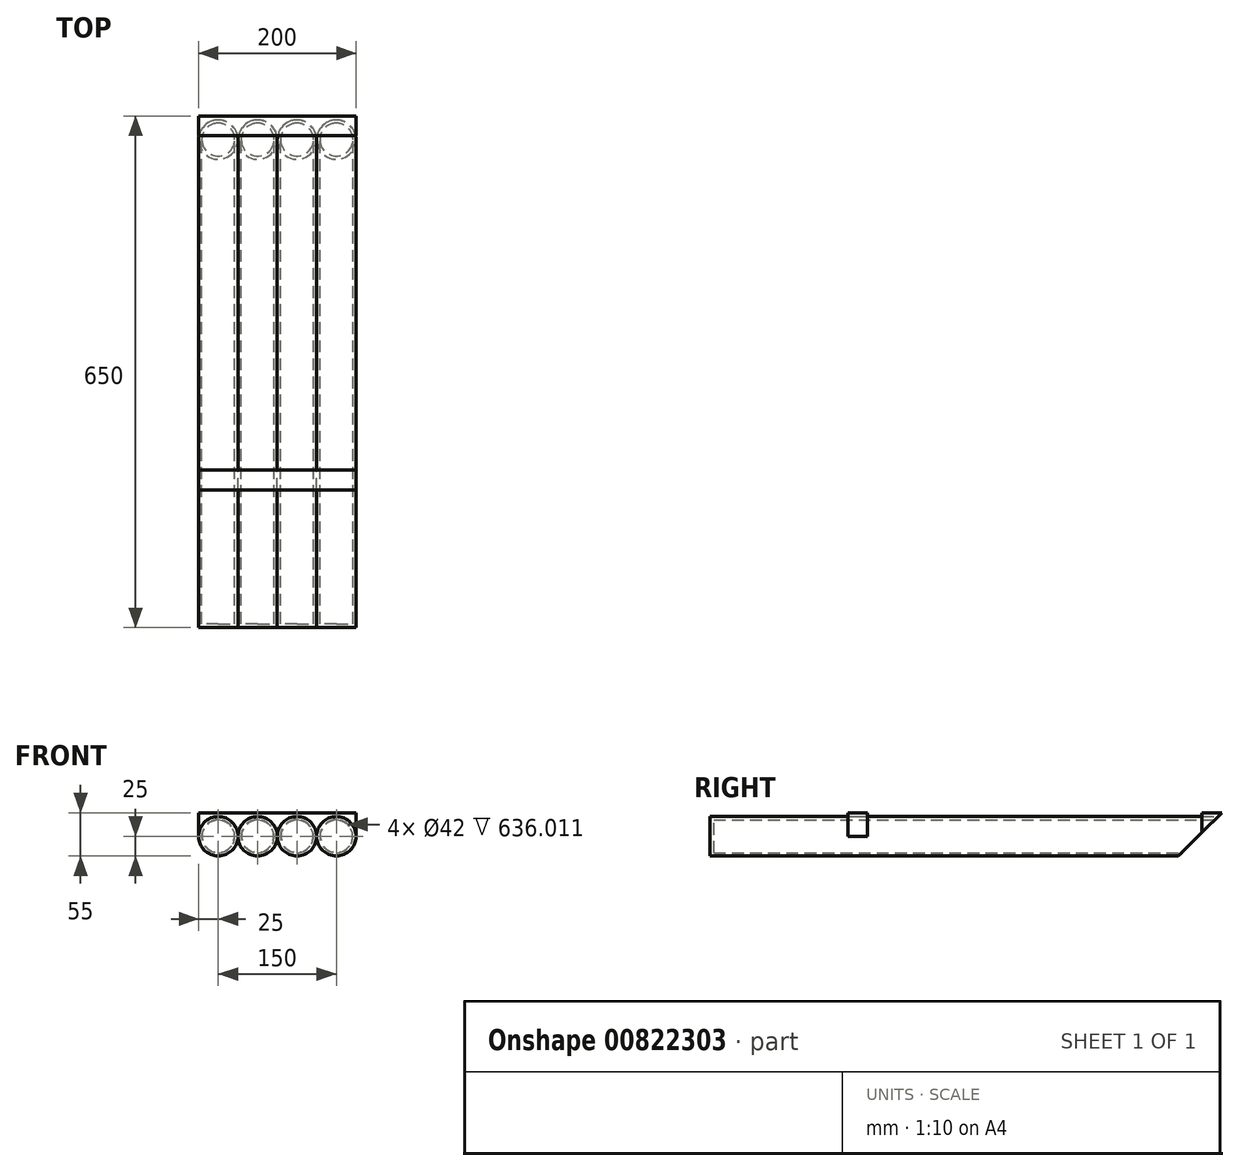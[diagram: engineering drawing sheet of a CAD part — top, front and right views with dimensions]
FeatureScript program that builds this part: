
annotation { "Feature Type Name" : "Feature", "Feature Type Description" : "" }
export const myFeature = defineFeature(function(context is Context, id is Id, definition is map)
    precondition{}
    {
        {
            var Q0;
            Q0=qCreatedBy(makeId("Front.planeOp"),FACE);
            var sketch = newSketch(context, id + "F0", { "sketchPlane" : qUnion([Q0])});
            skCircle(sketch, "E0", {"center": v(0, 0) * mm, "radius": 25 * mm});
            skCircle(sketch, "E1", {"center": v(50, 0) * mm, "radius": 25 * mm});
            skCircle(sketch, "E2", {"center": v(-50, 0) * mm, "radius": 25 * mm});
            skCircle(sketch, "E3", {"center": v(-100, 0) * mm, "radius": 25 * mm});
            skLineSegment(sketch, "E4", {"start": v(0, 0) * mm, "end": v(50, 0) * mm});
            skLineSegment(sketch, "E5", {"start": v(0, 0) * mm, "end": v(-50, 0) * mm});
            skLineSegment(sketch, "E6", {"start": v(-50, 0) * mm, "end": v(-100, 0) * mm});
            skCircle(sketch, "E7", {"center": v(50, 0) * mm, "radius": 21 * mm});
            skCircle(sketch, "E8", {"center": v(0, 0) * mm, "radius": 21 * mm});
            skCircle(sketch, "E9", {"center": v(-50, 0) * mm, "radius": 21 * mm});
            skCircle(sketch, "E10", {"center": v(-100, 0) * mm, "radius": 21 * mm});
            skSolve(sketch);
        }
        {
            var Q0;
            Q0 = qSketchRegion(id + "F0", true);
            extrude(context, id + "F1", {"entities" : qUnion([Q0]), "depth" : 700 * mm, "offsetDistance" : 25 * mm});
        }
        {
            var Q0;
            Q0=qCreatedBy(makeId("Front.planeOp"),FACE);
            cPlane(context, id + "F2", {"entities" : qUnion([Q0]), "cplaneType" : CPlaneType.OFFSET, "offset" : 50 * mm, "width" : 150 * mm, "height" : 150 * mm});
        }
        {
            var Q0;
            Q0=qCreatedBy(id+"F2.planeOp",FACE);
            var sketch = newSketch(context, id + "F3", { "sketchPlane" : qUnion([Q0])});
            skLineSegment(sketch, "E11", {"start": v(75, 0) * mm, "end": v(75, 25) * mm});
            skLineSegment(sketch, "E12", {"start": v(75, 25) * mm, "end": v(-125, 25) * mm});
            skLineSegment(sketch, "E13", {"start": v(-125, 25) * mm, "end": v(-125, 0) * mm});
            skCircle(sketch, "E14", {"center": v(0, 0) * mm, "radius": 25 * mm});
            skLineSegment(sketch, "E15", {"start": v(0, 0) * mm, "end": v(25, 0) * mm});
            skLineSegment(sketch, "E16", {"start": v(25, 0) * mm, "end": v(50, 0) * mm});
            skLineSegment(sketch, "E17", {"start": v(50, 0) * mm, "end": v(75, 0) * mm});
            skCircle(sketch, "E18", {"center": v(50, 0) * mm, "radius": 25 * mm});
            skLineSegment(sketch, "E19", {"start": v(0, 0) * mm, "end": v(-50, 0) * mm});
            skLineSegment(sketch, "E20", {"start": v(-50, 0) * mm, "end": v(-100, 0) * mm});
            skCircle(sketch, "E21", {"center": v(-50, 0) * mm, "radius": 25 * mm});
            skCircle(sketch, "E22", {"center": v(-100, 0) * mm, "radius": 25 * mm});
            skLineSegment(sketch, "E23", {"start": v(-125, 25) * mm, "end": v(-125, 30) * mm});
            skLineSegment(sketch, "E24", {"start": v(-125, 30) * mm, "end": v(75, 30) * mm});
            skLineSegment(sketch, "E25", {"start": v(75, 30) * mm, "end": v(75, 25) * mm});
            skSolve(sketch);
        }
        {
            var Q0;
            {var subQ0=sQuery(id+"F3.wireOp",EDGE,"E11");Q0=makeQuery(id+"F3.imprint","IMPRINT",FACE,{"disambiguationData":[TD([[makeQuery(id+"F3.imprint","IMPRINT",EDGE,{"derivedFrom":subQ0}),1.0]])]});}
            var Q1;
            {var subQ0=sQuery(id+"F3.wireOp",EDGE,"E21");var subQ1=sQuery(id+"F3.wireOp",EDGE,"E12");var subQ2=makeQuery(id+"F3.imprint","INTERSECT",VERTEX,{"derivedFrom":[subQ1,subQ0]});Q1=makeQuery(id+"F3.imprint","IMPRINT",FACE,{"disambiguationData":[TD([[makeQuery(id+"F3.imprint","IMPRINT",EDGE,{"disambiguationData":[TD([[subQ2,-1.0]])],"derivedFrom":subQ1}),1.0]])]});}
            var Q2;
            {var subQ0=sQuery(id+"F3.wireOp",EDGE,"E13");Q2=makeQuery(id+"F3.imprint","IMPRINT",FACE,{"disambiguationData":[TD([[makeQuery(id+"F3.imprint","IMPRINT",EDGE,{"derivedFrom":subQ0}),1.0]])]});}
            var Q3;
            {var subQ0=sQuery(id+"F3.wireOp",EDGE,"E18");var subQ1=sQuery(id+"F3.wireOp",EDGE,"E12");var subQ2=makeQuery(id+"F3.imprint","INTERSECT",VERTEX,{"derivedFrom":[subQ1,subQ0]});Q3=makeQuery(id+"F3.imprint","IMPRINT",FACE,{"disambiguationData":[TD([[makeQuery(id+"F3.imprint","IMPRINT",EDGE,{"disambiguationData":[TD([[subQ2,-1.0]])],"derivedFrom":subQ1}),1.0]])]});}
            var Q4;
            {var subQ0=sQuery(id+"F3.wireOp",EDGE,"E14");var subQ1=sQuery(id+"F3.wireOp",EDGE,"E12");var subQ2=makeQuery(id+"F3.imprint","INTERSECT",VERTEX,{"derivedFrom":[subQ1,subQ0]});Q4=makeQuery(id+"F3.imprint","IMPRINT",FACE,{"disambiguationData":[TD([[makeQuery(id+"F3.imprint","IMPRINT",EDGE,{"disambiguationData":[TD([[subQ2,-1.0]])],"derivedFrom":subQ1}),1.0]])]});}
            var Q5;
            {var subQ4=sQuery(id+"F3.wireOp",EDGE,"E23");Q5=makeQuery(id+"F3.imprint","IMPRINT",FACE,{"disambiguationData":[TD([[makeQuery(id+"F3.imprint","IMPRINT",EDGE,{"derivedFrom":subQ4}),-1.0]])]});}
            extrude(context, id + "F4", {"entities" : qUnion([Q0, Q1, Q2, Q3, Q4, Q5]), "depth" : 25 * mm, "offsetDistance" : 25 * mm});
        }
        {
            var Q0;
            Q0=qCreatedBy(makeId("Front.planeOp"),FACE);
            cPlane(context, id + "F5", {"entities" : qUnion([Q0]), "cplaneType" : CPlaneType.OFFSET, "offset" : 500 * mm, "width" : 150 * mm, "height" : 150 * mm});
        }
        {
            var Q0;
            Q0=qCreatedBy(id+"F5.planeOp",FACE);
            var sketch = newSketch(context, id + "F6", { "sketchPlane" : qUnion([Q0])});
            skLineSegment(sketch, "E26", {"start": v(75, 0) * mm, "end": v(75, 25) * mm});
            skLineSegment(sketch, "E27", {"start": v(75, 25) * mm, "end": v(-125, 25) * mm});
            skLineSegment(sketch, "E28", {"start": v(-125, 25) * mm, "end": v(-125, -4.17) * mm});
            skCircle(sketch, "E29", {"center": v(0, 0) * mm, "radius": 25 * mm});
            skLineSegment(sketch, "E30", {"start": v(0, 0) * mm, "end": v(25, 0) * mm});
            skLineSegment(sketch, "E31", {"start": v(25, 0) * mm, "end": v(50, 0) * mm});
            skLineSegment(sketch, "E32", {"start": v(50, 0) * mm, "end": v(75, 0) * mm});
            skCircle(sketch, "E33", {"center": v(50, 0) * mm, "radius": 25 * mm});
            skLineSegment(sketch, "E34", {"start": v(0, 0) * mm, "end": v(-50, 0) * mm});
            skLineSegment(sketch, "E35", {"start": v(-50, 0) * mm, "end": v(-100, 0) * mm});
            skCircle(sketch, "E36", {"center": v(-50, 0) * mm, "radius": 25 * mm});
            skCircle(sketch, "E37", {"center": v(-100, 0) * mm, "radius": 25 * mm});
            skLineSegment(sketch, "E38", {"start": v(-125, 25) * mm, "end": v(-125, 30) * mm});
            skLineSegment(sketch, "E39", {"start": v(-125, 30) * mm, "end": v(75, 30) * mm});
            skLineSegment(sketch, "E40", {"start": v(75, 30) * mm, "end": v(75, 25) * mm});
            skSolve(sketch);
        }
        {
            var Q0;
            {var subQ0=sQuery(id+"F6.wireOp",EDGE,"E29");var subQ1=sQuery(id+"F6.wireOp",EDGE,"E27");var subQ2=makeQuery(id+"F6.imprint","INTERSECT",VERTEX,{"derivedFrom":[subQ1,subQ0]});Q0=makeQuery(id+"F6.imprint","IMPRINT",FACE,{"disambiguationData":[TD([[makeQuery(id+"F6.imprint","IMPRINT",EDGE,{"disambiguationData":[TD([[subQ2,-1.0]])],"derivedFrom":subQ1}),1.0]])]});}
            var Q1;
            {var subQ4=sQuery(id+"F6.wireOp",EDGE,"E38");Q1=makeQuery(id+"F6.imprint","IMPRINT",FACE,{"disambiguationData":[TD([[makeQuery(id+"F6.imprint","IMPRINT",EDGE,{"derivedFrom":subQ4}),-1.0]])]});}
            var Q2;
            {var subQ0=sQuery(id+"F6.wireOp",EDGE,"E28");var subQ3=sQuery(id+"F6.wireOp",EDGE,"E37");var subQ5=makeQuery(id+"F6.imprint","INTERSECT",VERTEX,{"derivedFrom":[subQ0,subQ3]});Q2=makeQuery(id+"F6.imprint","IMPRINT",FACE,{"disambiguationData":[TD([[makeQuery(id+"F6.imprint","IMPRINT",EDGE,{"disambiguationData":[TD([[subQ5,1.0]])],"derivedFrom":subQ3}),-1.0]])]});}
            var Q3;
            {var subQ0=sQuery(id+"F6.wireOp",EDGE,"E26");Q3=makeQuery(id+"F6.imprint","IMPRINT",FACE,{"disambiguationData":[TD([[makeQuery(id+"F6.imprint","IMPRINT",EDGE,{"derivedFrom":subQ0}),1.0]])]});}
            var Q4;
            {var subQ0=sQuery(id+"F6.wireOp",EDGE,"E33");var subQ1=sQuery(id+"F6.wireOp",EDGE,"E27");var subQ2=makeQuery(id+"F6.imprint","INTERSECT",VERTEX,{"derivedFrom":[subQ1,subQ0]});Q4=makeQuery(id+"F6.imprint","IMPRINT",FACE,{"disambiguationData":[TD([[makeQuery(id+"F6.imprint","IMPRINT",EDGE,{"disambiguationData":[TD([[subQ2,-1.0]])],"derivedFrom":subQ1}),1.0]])]});}
            var Q5;
            {var subQ0=sQuery(id+"F6.wireOp",EDGE,"E36");var subQ1=sQuery(id+"F6.wireOp",EDGE,"E27");var subQ2=makeQuery(id+"F6.imprint","INTERSECT",VERTEX,{"derivedFrom":[subQ1,subQ0]});Q5=makeQuery(id+"F6.imprint","IMPRINT",FACE,{"disambiguationData":[TD([[makeQuery(id+"F6.imprint","IMPRINT",EDGE,{"disambiguationData":[TD([[subQ2,-1.0]])],"derivedFrom":subQ1}),1.0]])]});}
            extrude(context, id + "F7", {"entities" : qUnion([Q0, Q1, Q2, Q3, Q4, Q5]), "depth" : 25 * mm, "offsetDistance" : 25 * mm});
        }
        {
            var Q0;
            Q0=makeQuery(id+"F1.opExtrude","CAP_FACE",FACE,{"disambiguationData":[OSD([sQuery(id+"F0.wireOp",EDGE,"E3"),sQuery(id+"F0.wireOp",EDGE,"E10")])],"isStart":true});
            var sketch = newSketch(context, id + "F8", { "sketchPlane" : qUnion([Q0])});
            skCircle(sketch, "E41", {"center": v(100, 0) * mm, "radius": 21 * mm});
            skLineSegment(sketch, "E42", {"start": v(100, 0) * mm, "end": v(75, 0) * mm});
            skLineSegment(sketch, "E43", {"start": v(75, 0) * mm, "end": v(75, 53.83) * mm});
            skCircle(sketch, "E44.MirrorC", {"center": v(50, 0) * mm, "radius": 21 * mm});
            skLineSegment(sketch, "E45", {"start": v(50, 0) * mm, "end": v(25, 0) * mm});
            skLineSegment(sketch, "E46", {"start": v(25, 0) * mm, "end": v(25, 54.93) * mm});
            skCircle(sketch, "E47.MirrorC", {"center": v(0, 0) * mm, "radius": 21 * mm});
            skCircle(sketch, "E48.MirrorC", {"center": v(-50, 0) * mm, "radius": 21 * mm});
            skSolve(sketch);
        }
        {
            var Q0;
            Q0=makeQuery(id+"F1.opExtrude","CAP_FACE",FACE,{"disambiguationData":[OSD([sQuery(id+"F0.wireOp",EDGE,"E1"),sQuery(id+"F0.wireOp",EDGE,"E7")])],"isStart":false});
            var sketch = newSketch(context, id + "F9", { "sketchPlane" : qUnion([Q0])});
            skCircle(sketch, "E49", {"center": v(50, 0) * mm, "radius": 21 * mm});
            skLineSegment(sketch, "E50", {"start": v(50, 0) * mm, "end": v(25, 0) * mm});
            skLineSegment(sketch, "E51", {"start": v(25, 0) * mm, "end": v(25, 53.83) * mm});
            skCircle(sketch, "E52.MirrorC", {"center": v(0, 0) * mm, "radius": 21 * mm});
            skLineSegment(sketch, "E53", {"start": v(0, 0) * mm, "end": v(-25, 0) * mm});
            skLineSegment(sketch, "E54", {"start": v(-25, 0) * mm, "end": v(-25, 48.13) * mm});
            skCircle(sketch, "E55.MirrorC", {"center": v(-50, 0) * mm, "radius": 21 * mm});
            skCircle(sketch, "E56.MirrorC", {"center": v(-100, 0) * mm, "radius": 21 * mm});
            skSolve(sketch);
        }
        {
            var Q0;
            Q0 = qSketchRegion(id + "F9", true);
            extrude(context, id + "F10", {"entities" : qUnion([Q0]), "operationType" : NewBodyOperationType.ADD, "oppositeDirection" : true, "depth" : 5 * mm, "offsetDistance" : 25 * mm});
        }
        {
            var Q0;
            Q0=makeQuery(id+"F1.opExtrude","CAP_FACE",FACE,{"disambiguationData":[OSD([sQuery(id+"F0.wireOp",EDGE,"E2"),sQuery(id+"F0.wireOp",EDGE,"E9")])],"isStart":true});
            var Q1;
            Q1=makeQuery(id+"F1.opExtrude","CAP_FACE",FACE,{"disambiguationData":[OSD([sQuery(id+"F0.wireOp",EDGE,"E1"),sQuery(id+"F0.wireOp",EDGE,"E7")])],"isStart":true});
            var Q2;
            Q2=makeQuery(id+"F8.imprint","IMPRINT",FACE,{"disambiguationData":[TD([[makeQuery(id+"F8.imprint","IMPRINT",EDGE,{"derivedFrom":sQuery(id+"F8.wireOp",EDGE,"E41")}),1.0]])]});
            var Q3;
            Q3=makeQuery(id+"F1.opExtrude","CAP_FACE",FACE,{"disambiguationData":[OSD([sQuery(id+"F0.wireOp",EDGE,"E0"),sQuery(id+"F0.wireOp",EDGE,"E8")])],"isStart":true});
            extrude(context, id + "F11", {"entities" : qUnion([Q0, Q1, Q2, Q3]), "operationType" : NewBodyOperationType.REMOVE, "oppositeDirection" : true, "depth" : 50 * mm, "offsetDistance" : 25 * mm});
        }
        {
            var Q0;
            Q0=makeQuery(id+"F4.opExtrude","SWEPT_FACE",FACE,{"disambiguationData":[OSD([sQuery(id+"F3.wireOp",EDGE,"E13"),sQuery(id+"F3.wireOp",EDGE,"E23")])]});
            var sketch = newSketch(context, id + "F12", { "sketchPlane" : qUnion([Q0])});
            skLineSegment(sketch, "E57", {"start": v(50, 30) * mm, "end": v(50, -25) * mm});
            skLineSegment(sketch, "E58", {"start": v(50, -25) * mm, "end": v(105, -25) * mm});
            skLineSegment(sketch, "E59", {"start": v(105, -25) * mm, "end": v(50, 30) * mm});
            skSolve(sketch);
        }
        {
            var Q0;
            Q0 = qSketchRegion(id + "F12", true);
            extrude(context, id + "F13", {"entities" : qUnion([Q0]), "operationType" : NewBodyOperationType.REMOVE, "oppositeDirection" : true, "depth" : 200 * mm, "offsetDistance" : 25 * mm});
        }
    });
